# Revit family: Orinal Mediano
name_source: partatom
category: Aparatos sanitarios
revit_build: Autodesk Revit 2016 (Build: 20151007_0715(x64)
units: mm (PartAtom-declared; Revit-internal decimal feet)

## family parameters
Anfitrión = Muro
Compartido = No
Corte con vacíos al cargar = No
Cota de conector redondo = Diámetro de uso
Número OmniClass = 23.45.05.00
Punto de cálculo de habitación = No
Siempre vertical = Sí
Tipo de pieza = Normal
Título OmniClass = Sanitary Equipment

## types (1)
- Tipo 1
    Acabado = Brillante
    Alto Nominal = 430 mm
    Ancho Nominal = 325 mm  [stored 1.06627 ft]
    Característica = Orinal de colgar, Diseño compacto diseñado para espacios pequeños, Orinal de anillo cerrado con sistema integral de limpieza que garantiza mayor ingiene, Sistema de fijacion con grapas oculto, para instalación con sifón botella, incluye racor de entrada y grapas de fijación.
    Color = Blanco
    Consumo de Agua = 3.8 LPF
    Cumplimiento de Norma = ASME / ANSI A112.19.2
    Código de montaje = D2010210
    Descripción de la garantía = Garantia Corona Limintada de por vida para la porcelana
    Diámetro de conexión de entrada = 127 CM ( 1/2" ) - 1.88 (3/4")
    Diámetro de conexión sanitaria = 2.54 cm ( 1" )
    Duración Garantía Unidad = Años
    Fabricante = www.corona.com.co
    Forma = Ovalado
    Imagen de tipo = <Ninguno>
    Longitud Nominal = 300 mm  [stored 0.984252 ft]
    Material = Ceramica_Corona_Blanco
    Material Secundario = Plastico_Corona_Blanco
    Material de Fabricación = Porcelana Sanitaria Vitrificada
    Modelo = 088621001
    Nombre = Orinal de entrada superior Mediano
    Numero de Modelo = 088621001
    Presión máxima = 80 PSI.
    Presión mínima = 25 PSI.
    Responsable Garantia Partes = www.corona.com.co
    Tipo de Activo = Fijo

note: [stored X ft] marks values corroborated as IEEE doubles in the binary element streams (Revit-internal decimal feet)
